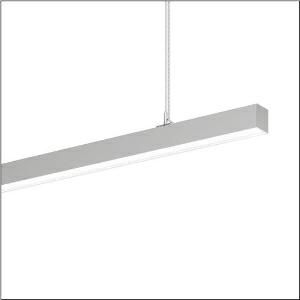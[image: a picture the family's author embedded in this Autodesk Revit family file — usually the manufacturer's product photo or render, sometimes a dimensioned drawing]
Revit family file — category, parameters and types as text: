
# Revit family: silica_r__21_51mx33tctds_657e
name_source: partatom
category: Lighting Fixtures
units: mm (PartAtom-declared; Revit-internal decimal feet)

## family parameters
Cut with Voids When Loaded = No
Host = Face
Light Source = No
Part Type = Normal
Room Calculation Point = No
Round Connector Dimension = Use Diameter
Shared = No

## types (1)
- --- (1 x LED, 14340 lm, 134.7 W, 6500K)
    Apparent Load = 135 VA
    CIE Flux Codes = 78 96 99 56 100
    Color Rendering = 80
    Color Temperature = 6500K
    Default Elevation = 1800 mm
    Description = Silica® 21, office luminaire, primary optical cover: prismatic diffuser, of PMMA, CAT 2 (L<= 3000cd/m²), light emission: direct/indirect distribution, primary light characteristic: symmetric, installation type: suspended mounting, LED, rated luminous flux: 14.340lm, luminous efficacy: 101lm/W, light colour: 8tw, colour temperature: 2700..6500K, control gear: ECG DALI, with terminal, 3+2-pole, max. 2.5mm², mains connection: 220..240V, AC, 50/60Hz, rated input power: 141.4W, luminaire housing, of aluminium, metallic grey (RAL 9006), length: 3.004mm, width: 53mm, height: 53mm, protection rating (complete): IP20, insulation class (complete): insulation class I (protective earthing), certification: CE, permissible operating ambient temperature: 0..+35°C, standard: EN 50419, packaging unit: 1 piece
    Height = 53 mm
    Lamp = 1 x LED
    Lamp Light Flux = 14340 lm
    Lamp Power = 134.7 W
    Lamp count = 1
    Length = 3004 mm
    Luminous efficacy = 106 lm/W
    Manufacturer = Siteco
    ModVariant = No
    Model = 51MX33TCTDS
    Mounting Place = Ceiling
    Mounting Type = Pendant
    Number of Poles = 1
    OnlyDefault = Yes
    Power Factor = 1
    Product Name = Silica® 21
    Product group = office luminaire | ceiling pendant
    ProductGroupID = 902
    Protection Class = Protection class I
    Protection Degree = IP 20
    RLX_Detail_Level = 1
    RLX_Emergency_Light_Flux = 0 lm
    RLX_Emergency_Type = 0
    RLX_Emergency_Type_DB = No
    RlxData = <blob elided: 20101 chars, md5=a46455a1>
    Socket = socket
    Standby Power = 0 W
    System Light Flux = 14340 lm
    System Power = 135 W
    Type Comments = individual setting
    Type Image = l_1335864.jpg
    URL = http://relux.com
    VarID = @adj_109537
    Voltage = 0 V
    Weight = 0.00 kg
    Width = 53 mm

## geometry (parser evidence)
native form markers: Blend x4, Sweep x14
no freeform markers — native parametric forms only
